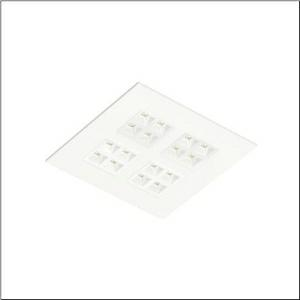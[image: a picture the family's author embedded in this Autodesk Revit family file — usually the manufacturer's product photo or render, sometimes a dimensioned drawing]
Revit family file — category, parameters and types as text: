
# Revit family: silica_r__31_square_51my6ndu44wa_4dbb
name_source: partatom
category: Lighting Fixtures
units: mm (PartAtom-declared; Revit-internal decimal feet)

## family parameters
Cut with Voids When Loaded = No
Host = Face
Light Source = No
Part Type = Normal
Room Calculation Point = No
Round Connector Dimension = Use Diameter
Shared = No

## types (1)
- --- (1 x LED, 6640 lm, 38.5 W, 4000K)
    Apparent Load = 39 VA
    CIE Flux Codes = 81 99 100 100 100
    Color Rendering = 80
    Color Temperature = 4000K
    Default Elevation = 1800 mm
    Description = Silica® 31 Square, office luminaire, primary light control with lens, of PMMA, primary anti-glare with reflector, of PC, white, light emission: direct distribution, primary light characteristic: symmetric, installation type: lay-in mounting, LED, rated luminous flux: 4.570lm, luminous efficacy: 176lm/W, light colour: 840, colour temperature: 4000K, control gear: DALI 2, Multilumen, with terminal, 5-pole, mains connection: 220..240V, AC, 50/60Hz, rated input power: 26W, luminaire housing, of sheet steel, coated, traffic white (RAL 9016), module: M625, length: 620mm, width: 620mm, height: 43mm, protection rating (complete): IP20, insulation class (complete): insulation class II (safety insulation), certification: CE, impact resistance: IK03, permissible operating ambient temperature: -20..+35°C, standard: EN 50419, packaging unit: 1 piece
    Height = 0 mm  [stored 0 ft]
    Lamp = 1 x LED
    Lamp Light Flux = 6640 lm
    Lamp Power = 38.5 W
    Lamp count = 1
    Length = 620 mm
    Luminous efficacy = 172 lm/W
    Manufacturer = Siteco
    ModVariant = No
    Model = 51MY6NDU44WA
    Mounting Place = Ceiling
    Mounting Type = Recessed
    Number of Poles = 1
    OnlyDefault = Yes
    Power Factor = 1
    Product Name = Silica® 31 Square
    Product group = office luminaire | ceiling recessed
    ProductGroupID = 400
    Protection Class = Protection class II
    Protection Degree = IP 20
    RLX_Detail_Level = 1
    RLX_Emergency_Light_Flux = 0 lm
    RLX_Emergency_Type = 0
    RLX_Emergency_Type_DB = No
    RlxData = <blob elided: 28137 chars, md5=faea4f79>
    Socket = socket
    Standby Power = 0 W
    System Light Flux = 6640 lm
    System Power = 39 W
    Type Comments = factory setting: luminous flux: 100 % | (OFF | OFF | OFF | OFF) | 1050 mA
    Type Image = l_1313651.jpg
    URL = http://relux.com
    VarID = @adj_056535
    Voltage = 0 V
    Weight = 0.00 kg
    Width = 620 mm

note: [stored X ft] marks values corroborated as IEEE doubles in the binary element streams (Revit-internal decimal feet)

## geometry (parser evidence)
native form markers: Blend x4, Sweep x10
no freeform markers — native parametric forms only
